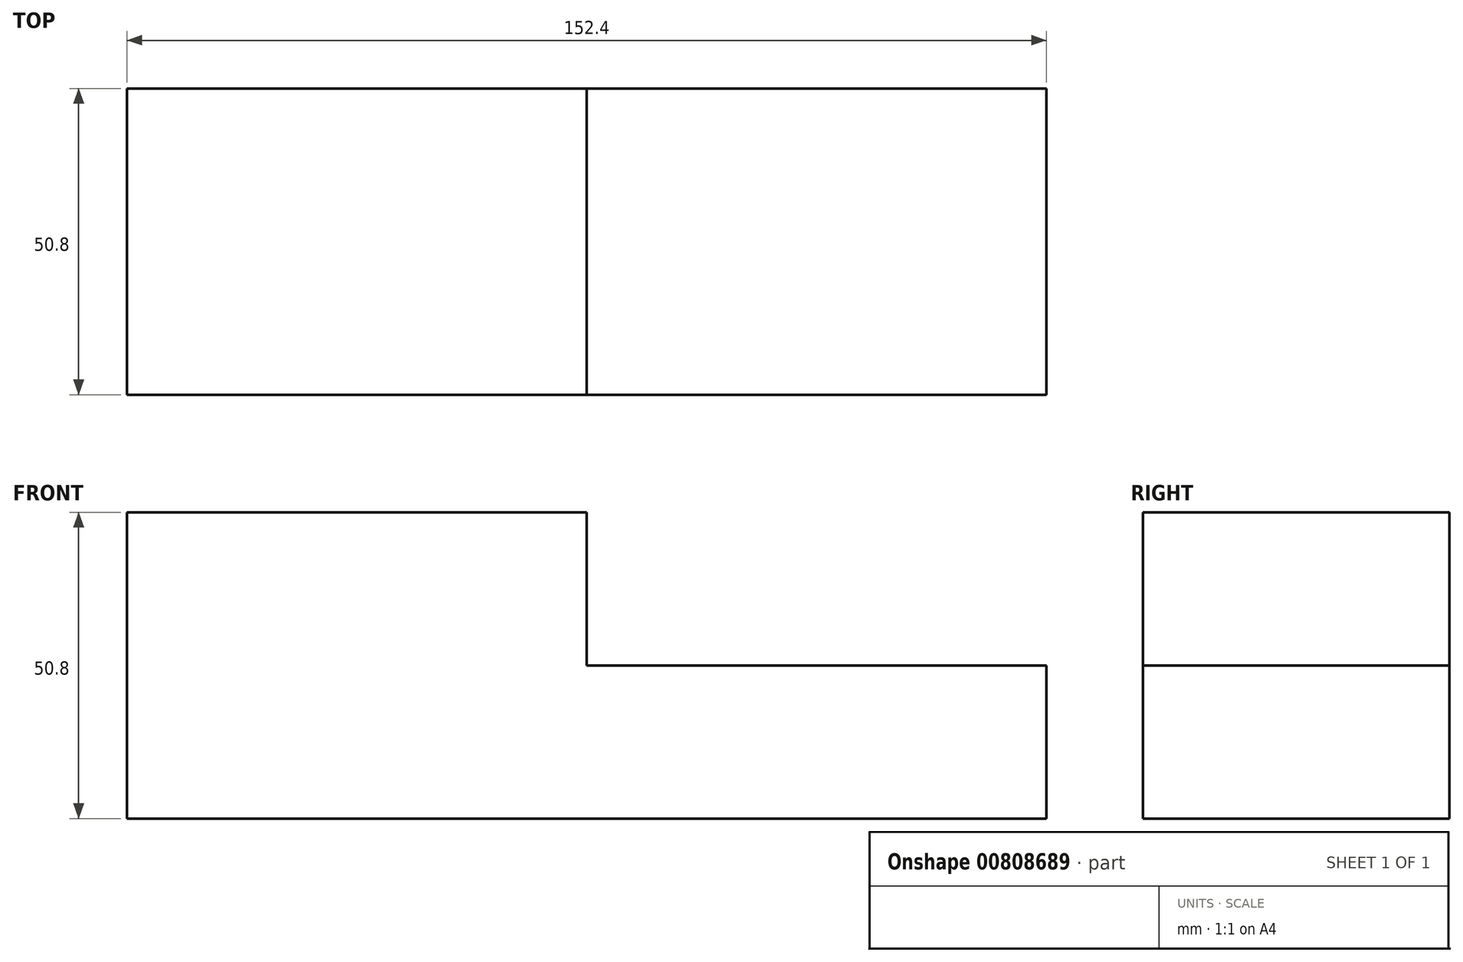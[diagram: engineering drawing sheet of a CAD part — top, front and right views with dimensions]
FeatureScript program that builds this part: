
annotation { "Feature Type Name" : "Feature", "Feature Type Description" : "" }
export const myFeature = defineFeature(function(context is Context, id is Id, definition is map)
    precondition{}
    {
        {
            var Q0;
            Q0=qCreatedBy(makeId("Front.planeOp"),FACE);
            var sketch = newSketch(context, id + "F0", { "sketchPlane" : qUnion([Q0])});
            skLineSegment(sketch, "E0", {"start": v(-76.2, 0) * mm, "end": v(-76.2, 50.8) * mm});
            skLineSegment(sketch, "E1", {"start": v(-76.2, 50.8) * mm, "end": v(0, 50.8) * mm});
            skLineSegment(sketch, "E2", {"start": v(0, 50.8) * mm, "end": v(0, 25.4) * mm});
            skLineSegment(sketch, "E3", {"start": v(0, 25.4) * mm, "end": v(76.2, 25.4) * mm});
            skLineSegment(sketch, "E4", {"start": v(76.2, 25.4) * mm, "end": v(76.2, 0) * mm});
            skLineSegment(sketch, "E5", {"start": v(76.2, 0) * mm, "end": v(-76.2, 0) * mm});
            skSolve(sketch);
        }
        {
            var Q0;
            Q0=makeQuery(id+"F0.imprint","IMPRINT",FACE,{"disambiguationData":[TD([[makeQuery(id+"F0.imprint","IMPRINT",EDGE,{"derivedFrom":sQuery(id+"F0.wireOp",EDGE,"E0")}),-1.0]])]});
            extrude(context, id + "F1", {"entities" : qUnion([Q0]), "depth" : 50.8 * mm, "offsetDistance" : 25.4 * mm});
        }
    });
